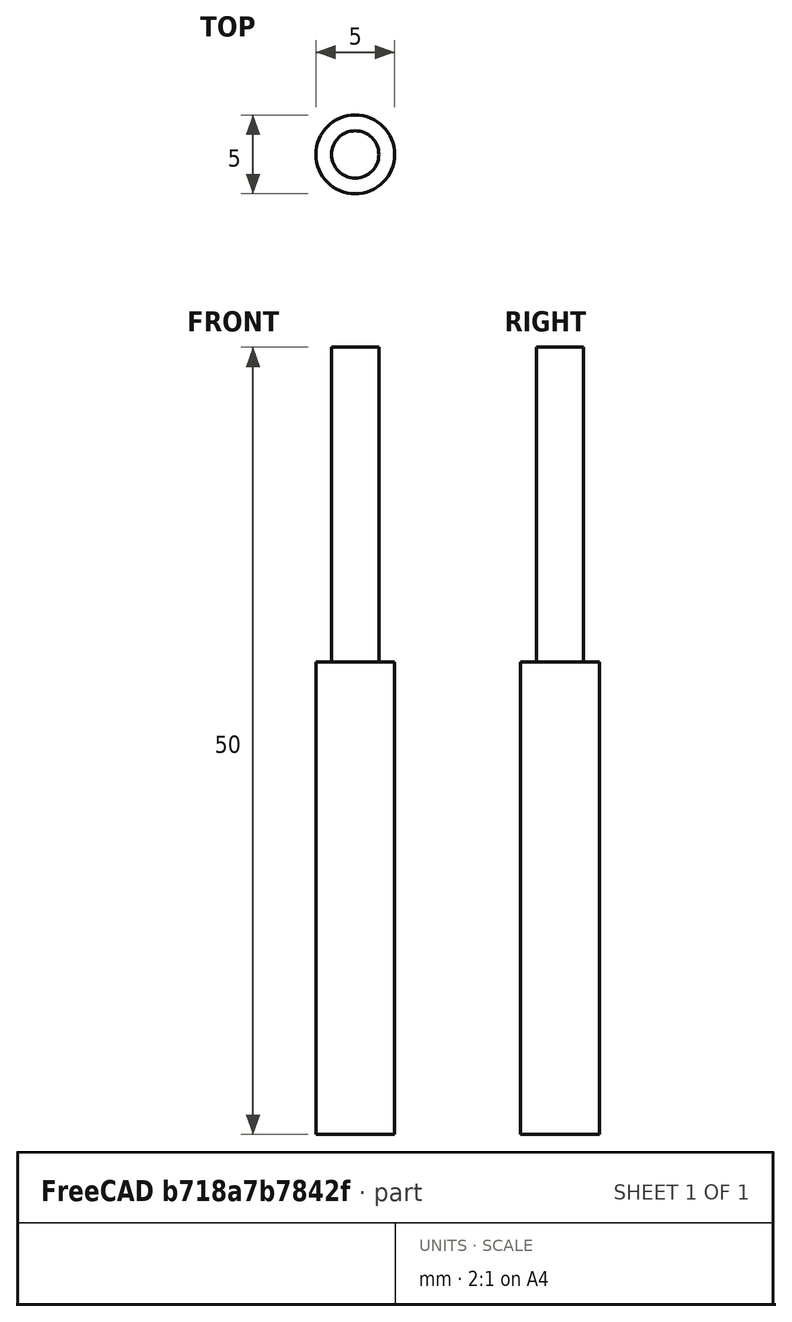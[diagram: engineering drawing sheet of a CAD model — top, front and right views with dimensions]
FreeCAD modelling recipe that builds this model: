
FCSTD DOCUMENT  (FreeCAD 1.0R39109 (Git))
Label: reamer
License: All rights reserved
LicenseURL: http://en.wikipedia.org/wiki/All_rights_reserved
objects: Sketcher::SketchObject×1, PartDesign::Revolution×1, App::FeaturePython×1, PartDesign::Body×1
note: 6 computed .brp shape members not serialized (recipe doc carries the construction recipe); baked Part::Feature solids carry a one-line shape summary decoded from their .brp

FEATURE [Sketcher::SketchObject] Sketch
  ArcFitTolerance = 0
  AttachmentSupport = -> [XZ_Plane]
  FullyConstrained = true
  MakeInternals = false
  MapMode = 5
  Placement = pos=(0,0,0) rot=(1,0,0;1.5708rad)
  expr: Constraints[10] = <<Attributes>>.Length
  expr: Constraints[16] = <<Attributes>>.ShankDiameter
  expr: Constraints[18] = <<Attributes>>.CuttingEdgeHeight
  expr: Constraints[9] = <<Attributes>>.Diameter
  sketch-geometry (8):
    g0: LineSegment StartX=0 StartY=50 StartZ=0 EndX=0 EndY=0 EndZ=0
    g1: LineSegment StartX=0 StartY=0 StartZ=0 EndX=2.5 EndY=0 EndZ=0
    g2: LineSegment StartX=2.5 StartY=0 StartZ=0 EndX=2.5 EndY=30 EndZ=0
    g3: LineSegment StartX=1.5 StartY=50 StartZ=0 EndX=0 EndY=50 EndZ=0
    g4: LineSegment [constr] StartX=2.5 StartY=0 StartZ=0 EndX=-2.5 EndY=0 EndZ=0
    g5: LineSegment StartX=1.5 StartY=29.99 StartZ=0 EndX=2.5 EndY=30 EndZ=0
    g6: LineSegment StartX=1.5 StartY=50 StartZ=0 EndX=1.5 EndY=29.99 EndZ=0
    g7: LineSegment [constr] StartX=-1.5 StartY=50 StartZ=0 EndX=1.5 EndY=50 EndZ=0
  constraints (21):
    c: Vertical(g0)
    c: Coincident(g0,g1)
    c: Horizontal(g1)
    c: Coincident(g1,g2)
    c: Vertical(g2)
    c: Horizontal(g3)
    c: Coincident(g0,g3)
    c: Coincident(g4,g1)
    c: Symmetric(g1,g4,g0)
    c: DistanceX(g4,g4) = 5
    c: DistanceY(g2,g3) = 50
    c: Coincident(g2,g5)
    c: Vertical(g6)
    c: Coincident(g3,g6)
    c: Symmetric(g7,g7,g0)
    c: Coincident(g7,g3)
    c: DistanceX(g7,g7) = 3
    c: Coincident(g5,g6)
    c: DistanceY(g2) = 30
    c: Coincident(g0,g-1)
    c: DistanceY(g5,g2) = 0.01
FEATURE [PartDesign::Revolution] Revolution
  AllowMultiFace = false
  Angle = 360
  Angle2 = 60
  Axis = (0,2e-16,1)
  Base = (0,0,0)
  Placement = pos=(0,0,0) rot=(1,0,0;1.5708rad)
  Profile = -> Sketch
  ReferenceAxis = -> Sketch [V_Axis]
  Reversed = true
  Suppressed = false
  Type = 0
FEATURE [App::FeaturePython] PropertyBag  label="Attributes"  # WARN: FeaturePython — macro-defined, semantics opaque (R4)
  CustomPropertyGroups = 0
  CuttingEdgeHeight = 30
  Diameter = 5
  Length = 50
  ShankDiameter = 3
FEATURE [PartDesign::Body] Body  label="Reamer"
  AllowCompound = false
  Group = -> [Sketch,Revolution,PropertyBag]
  Origin = -> Origin
  Tip = -> Revolution
